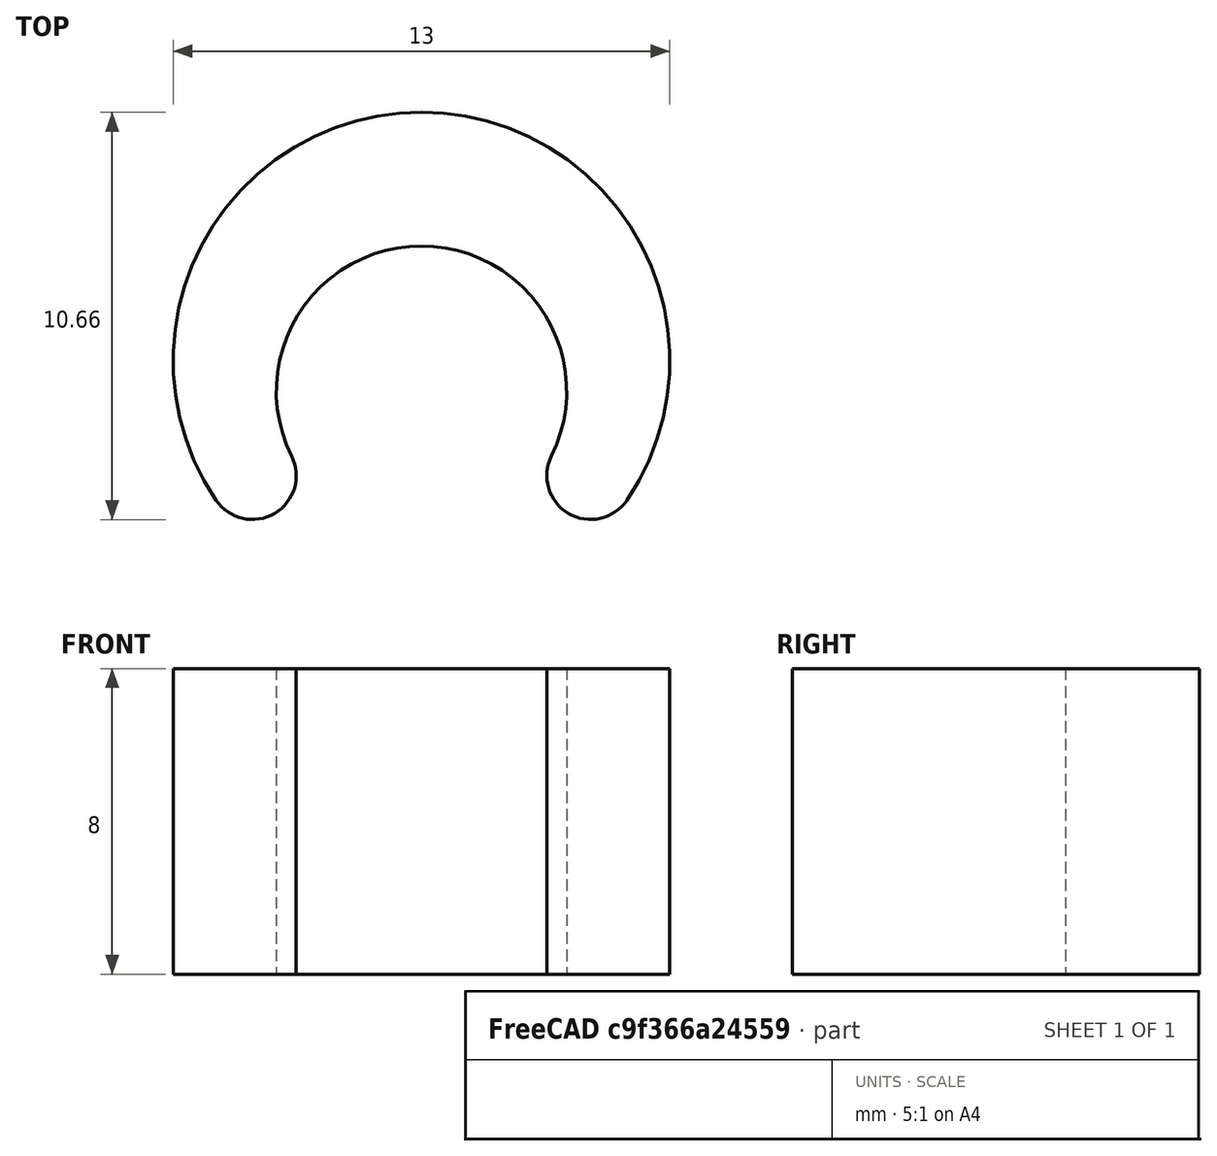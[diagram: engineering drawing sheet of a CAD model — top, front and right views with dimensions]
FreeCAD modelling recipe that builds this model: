
FCSTD DOCUMENT  (FreeCAD 0.20R24992 (Git))
Label: stopper-1
License: All rights reserved
LicenseURL: http://en.wikipedia.org/wiki/All_rights_reserved
objects: Sketcher::SketchObject×1, PartDesign::Pad×1, PartDesign::Body×1
note: 4 computed .brp shape members not serialized (recipe doc carries the construction recipe); baked Part::Feature solids carry a one-line shape summary decoded from their .brp

FEATURE [Sketcher::SketchObject] Sketch
  FullyConstrained = true
  MapMode = 5
  Support = -> [XY_Plane]
  sketch-geometry (5):
    g0: ArcOfCircle CenterX=0 CenterY=0 CenterZ=0 NormalX=0 NormalY=0 NormalZ=1 AngleXU=0 Radius=3.8 StartAngle=5.82023 EndAngle=9.88773
    g1: ArcOfCircle CenterX=-4.42655 CenterY=-2.20944 CenterZ=0 NormalX=0 NormalY=0 NormalZ=1 AngleXU=0 Radius=1.14732 StartAngle=3.73867 EndAngle=6.74614
    g2: ArcOfCircle CenterX=4.42655 CenterY=-2.20944 CenterZ=0 NormalX=0 NormalY=0 NormalZ=1 AngleXU=0 Radius=1.14732 StartAngle=2.67864 EndAngle=5.6861
    g3: LineSegment StartX=-3.4 StartY=-1.69706 StartZ=0 EndX=3.4 EndY=-1.69706 EndZ=0
    g4: ArcOfCircle CenterX=0 CenterY=0.8 CenterZ=0 NormalX=0 NormalY=0 NormalZ=1 AngleXU=0 Radius=6.5 StartAngle=5.6861 EndAngle=10.0219
  constraints (13):
    c: Coincident(g0,g-1)
    c: Coincident(g3,g0)
    c: Coincident(g3,g0)
    c: Horizontal(g3)
    c: Tangent(g2,g0) = 1.5708
    c: Tangent(g1,g0) = 1.5708
    c: Radius(g0) = 3.8
    c: Radius(g4) = 6.5
    c: PointOnObject(g4,g-2)
    c: DistanceY(g0,g4) = 0.8
    c: Tangent(g4,g1) = -1.5708
    c: Tangent(g4,g2) = -1.5708
    c: DistanceX(g0,g0) = 6.8
FEATURE [PartDesign::Pad] Pad
  Direction = (0,0,1)
  Length = 8
  Length2 = 100
  Profile = -> Sketch
  Type = 0
FEATURE [PartDesign::Body] Body
  Group = -> [Sketch,Pad]
  Origin = -> Origin
  Tip = -> Pad
